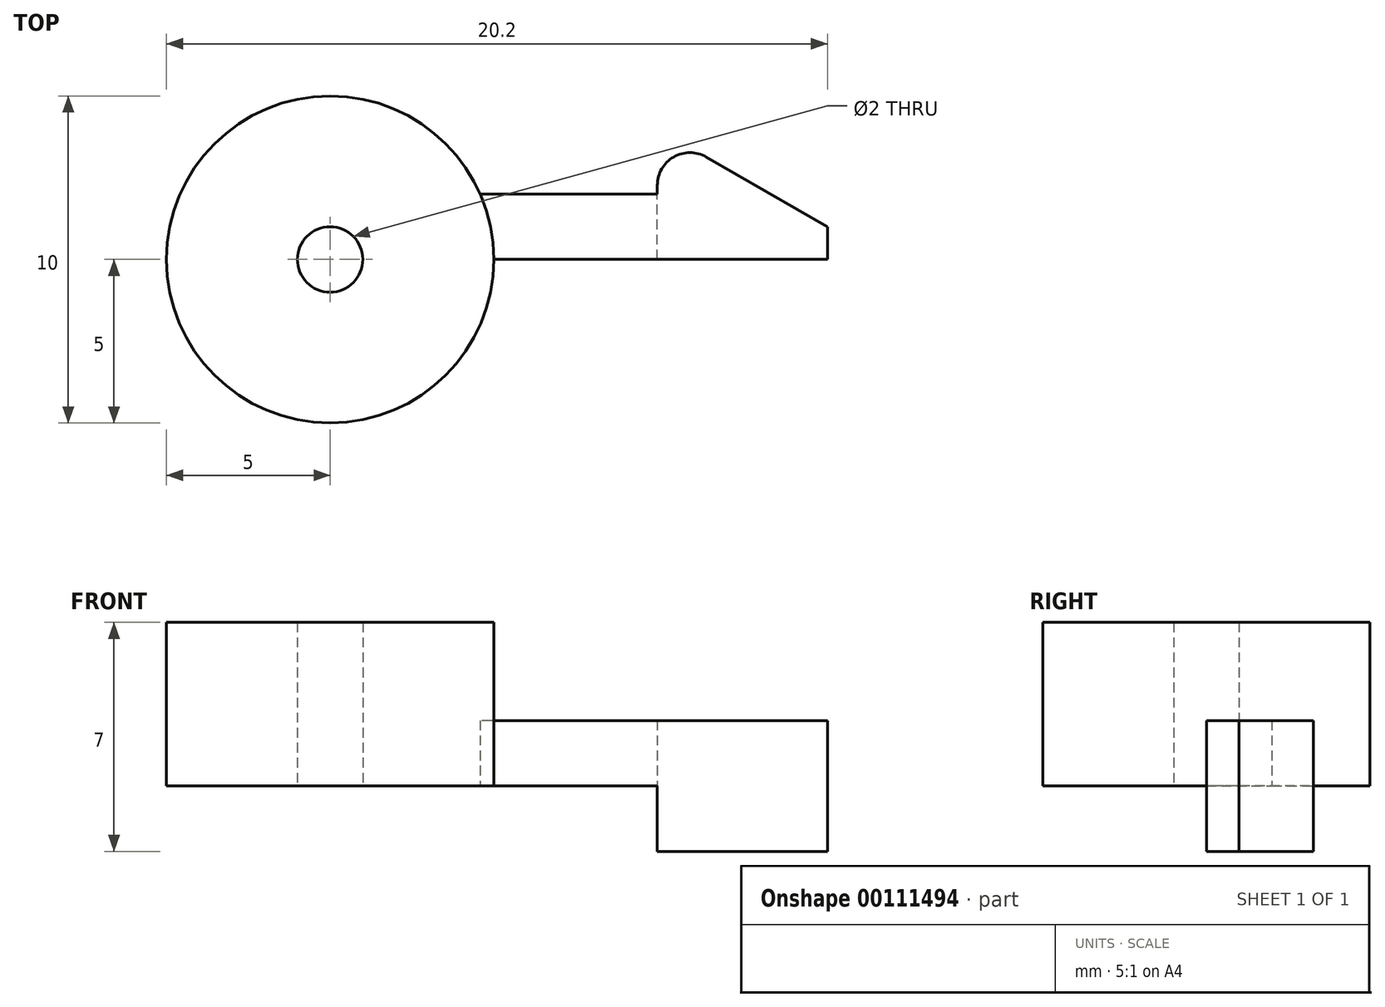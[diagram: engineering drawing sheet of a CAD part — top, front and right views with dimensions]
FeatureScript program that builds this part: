
annotation { "Feature Type Name" : "Feature", "Feature Type Description" : "" }
export const myFeature = defineFeature(function(context is Context, id is Id, definition is map)
    precondition{}
    {
        {
            var Q0;
            Q0=qCreatedBy(makeId("Top.planeOp"),FACE);
            var sketch = newSketch(context, id + "F0", { "sketchPlane" : qUnion([Q0])});
            skCircle(sketch, "E0", {"center": v(0, 0) * mm, "radius": 5 * mm});
            skLineSegment(sketch, "E1", {"start": v(5, 0) * mm, "end": v(10, 0) * mm});
            skLineSegment(sketch, "E2", {"start": v(10, 0) * mm, "end": v(10, 4) * mm});
            skLineSegment(sketch, "E3", {"start": v(10, 0) * mm, "end": v(15.2, 0) * mm});
            skLineSegment(sketch, "E4", {"start": v(15.2, 0) * mm, "end": v(15.2, 1) * mm});
            skLineSegment(sketch, "E5", {"start": v(10, 4) * mm, "end": v(15.2, 1) * mm});
            skLineSegment(sketch, "E6", {"start": v(10, 2) * mm, "end": v(4.58, 2) * mm});
            skSolve(sketch);
        }
        {
            var Q0;
            {var subQ0=sQuery(id+"F0.wireOp",EDGE,"E1");Q0=makeQuery(id+"F0.imprint","IMPRINT",FACE,{"disambiguationData":[TD([[makeQuery(id+"F0.imprint","IMPRINT",EDGE,{"derivedFrom":subQ0}),1.0]])]});}
            extrude(context, id + "F1", {"entities" : qUnion([Q0]), "depth" : 2 * mm});
        }
        {
            var Q0;
            {var subQ0=sQuery(id+"F0.wireOp",EDGE,"E0");var subQ1=makeQuery(id+"F0.imprint","INTERSECT",VERTEX,{"derivedFrom":[subQ0,sQuery(id+"F0.wireOp",EDGE,"E1")]});Q0=makeQuery(id+"F0.imprint","IMPRINT",FACE,{"disambiguationData":[TD([[makeQuery(id+"F0.imprint","IMPRINT",EDGE,{"disambiguationData":[TD([[subQ1,-1.0]])],"derivedFrom":subQ0}),1.0]])]});}
            extrude(context, id + "F2", {"entities" : qUnion([Q0]), "operationType" : NewBodyOperationType.ADD, "depth" : 5 * mm});
        }
        {
            var Q0;
            {var subQ0=sQuery(id+"F0.wireOp",EDGE,"E3");Q0=makeQuery(id+"F0.imprint","IMPRINT",FACE,{"disambiguationData":[TD([[makeQuery(id+"F0.imprint","IMPRINT",EDGE,{"derivedFrom":subQ0}),1.0]])]});}
            extrude(context, id + "F3", {"entities" : qUnion([Q0]), "operationType" : NewBodyOperationType.ADD, "endBound" : BoundingType.SYMMETRIC, "depth" : 4 * mm});
        }
        {
            var Q0;
            Q0=makeQuery(id+"F3.opExtrude","SWEPT_EDGE",EDGE,{"disambiguationData":[OSD([sQuery(id+"F0.wireOp",EDGE,"E2"),sQuery(id+"F0.wireOp",EDGE,"E5")])]});
            fillet(context, id + "F4", {"entities" : qUnion([Q0]), "radius" : 1 * mm, "tangentPropagation" : true, "allowEdgeOverflow" : false});
        }
        {
            var Q0;
            Q0=sQuery(id+"F0.wireOp",VERTEX,"E0.center");
            var Q1;
            Q1=makeQuery(id+"F1.opExtrude","SWEPT_BODY",BODY,{"disambiguationData":[OSD([sQuery(id+"F0.wireOp",EDGE,"E0"),sQuery(id+"F0.wireOp",EDGE,"E1"),sQuery(id+"F0.wireOp",EDGE,"E2"),sQuery(id+"F0.wireOp",EDGE,"E6")])]});
            hole(context, id + "F5", {"style" : HoleStyle.SIMPLE, "endStyle" : HoleEndStyle.THROUGH, "oppositeDirection" : true, "holeDiameter" : 2 * mm, "locations" : qUnion([Q0]), "scope" : qUnion([Q1]), "isTappedThrough" : true});
        }
    });
